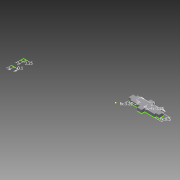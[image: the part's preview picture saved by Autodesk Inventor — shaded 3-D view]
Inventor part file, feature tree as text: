
AUTODESK INVENTOR PART (.ipt)
format: ipt  version: 2013 (Build 170138000, 138)  size: 119,296 bytes
history: native  units: mm
features: extrude x4, other x2, sketch x1
ambient origin geometry x8: Origin, YZ Plane, XZ Plane, XY Plane, X Axis, Y Axis, Z Axis, Center Point
feature tree (7):
  other  "Blocks"
  sketch  "Sketch1"  dims[d0=3.0mm d2=3.0mm d3=0.1mm d7=22.5mm d8=12.4mm d9=4.5mm d10=4.5mm d11=2.0mm d12=2.0mm d58=27.0mm d59=8.5mm d60=3.25mm d61=0.0mm d62=5.0mm d63=3.25mm d64=3.25mm d65=5.0mm d66=3.25mm d67=0.0mm d68=3.25mm d69=0.0mm d70=3.25mm d71=0.0mm]
  extrude  "Extrusion5"  Depth=3.0mm
  extrude  "Extrusion6"  Depth=27.0mm
  extrude  "Extrusion7"  Depth=8.5mm
  extrude  "Extrusion8"  Depth=3.25mm
  other  "Block1"
